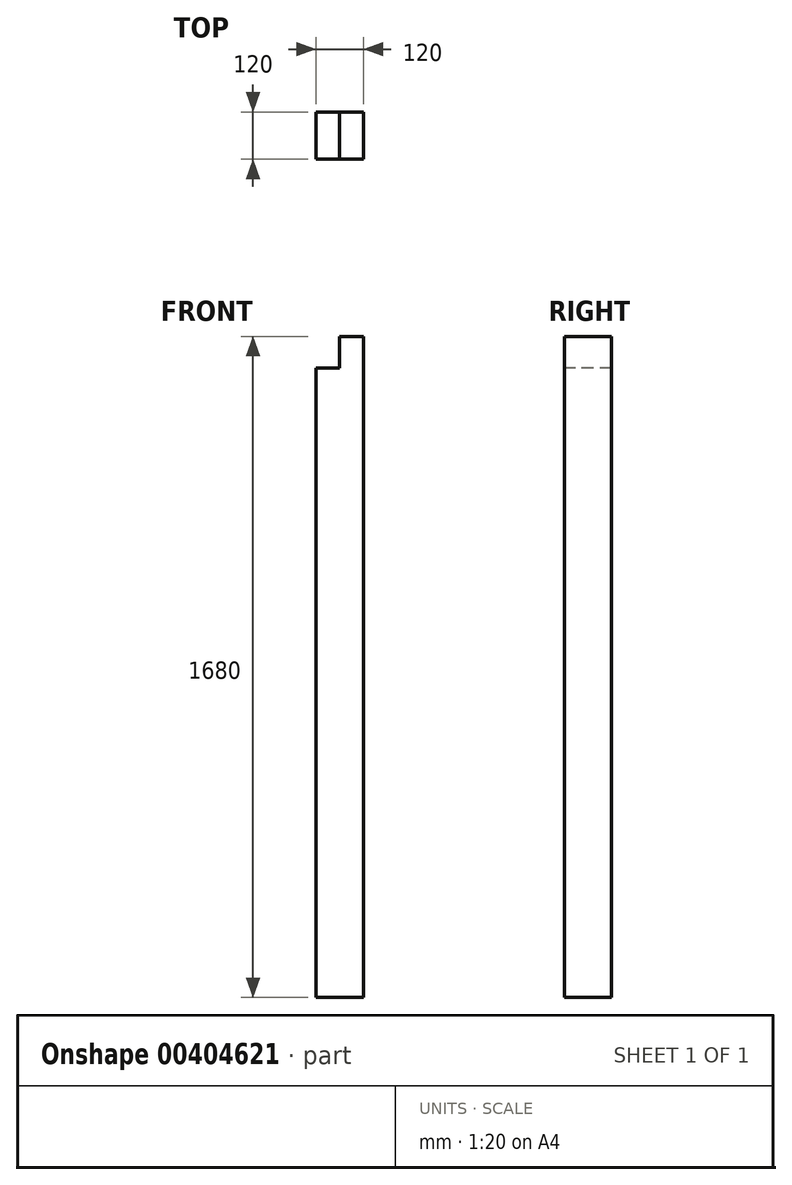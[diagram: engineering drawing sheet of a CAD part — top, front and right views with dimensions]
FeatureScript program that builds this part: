
annotation { "Feature Type Name" : "Feature", "Feature Type Description" : "" }
export const myFeature = defineFeature(function(context is Context, id is Id, definition is map)
    precondition{}
    {
        {
            assignVariable(context, id + "F0", {"name" : "hLounge", "anyValue" : 1600});
        }
        {
            assignVariable(context, id + "F1", {"name" : "hBalken", "anyValue" : 80});
        }
        {
            var Q0;
            Q0=qCreatedBy(makeId("Top.planeOp"),FACE);
            var sketch = newSketch(context, id + "F2", { "sketchPlane" : qUnion([Q0])});
            skLineSegment(sketch, "E0.bottom", {"start": v(-60, 60) * mm, "end": v(60, 60) * mm});
            skLineSegment(sketch, "E0.top", {"start": v(-60, -60) * mm, "end": v(60, -60) * mm});
            skLineSegment(sketch, "E0.left", {"start": v(-60, 60) * mm, "end": v(-60, -60) * mm});
            skLineSegment(sketch, "E0.right", {"start": v(60, 60) * mm, "end": v(60, -60) * mm});
            skSolve(sketch);
        }
        {
            var Q0;
            Q0=makeQuery(id+"F2.imprint","IMPRINT",FACE,{"disambiguationData":[TD([[makeQuery(id+"F2.imprint","IMPRINT",EDGE,{"derivedFrom":sQuery(id+"F2.wireOp",EDGE,"E0.bottom")}),-1.0]])]});
            extrude(context, id + "F3", {"entities" : qUnion([Q0]), "depth" : (getVariable(context, 'hLounge') + getVariable(context, 'hBalken')) * mm});
        }
        {
            var Q0;
            Q0=makeQuery(id+"F3.opExtrude","SWEPT_FACE",FACE,{"disambiguationData":[OSD([sQuery(id+"F2.wireOp",EDGE,"E0.top")])]});
            var sketch = newSketch(context, id + "F4", { "sketchPlane" : qUnion([Q0])});
            skLineSegment(sketch, "E1.bottom", {"start": v(-60, 1680) * mm, "end": v(0, 1680) * mm});
            skLineSegment(sketch, "E1.top", {"start": v(-60, 1600) * mm, "end": v(0, 1600) * mm});
            skLineSegment(sketch, "E1.left", {"start": v(-60, 1680) * mm, "end": v(-60, 1600) * mm});
            skLineSegment(sketch, "E1.right", {"start": v(0, 1680) * mm, "end": v(0, 1600) * mm});
            skSolve(sketch);
        }
        {
            var Q0;
            Q0=qSketchRegion(id+"F4",true);
            extrude(context, id + "F5", {"entities" : qUnion([Q0]), "operationType" : NewBodyOperationType.REMOVE, "endBound" : BoundingType.UP_TO_NEXT, "oppositeDirection" : true, "depth" : 25 * mm});
        }
    });
